# Revit family: Landscaping_Other_Axelent_Lock-Rail
name_source: partatom
category: Furniture
revit_build: Autodesk Revit 2018 (Build: 20170223_1515(x64)
units: mm (PartAtom-declared; Revit-internal decimal feet)

## family parameters
Always vertical = Yes
Cut with Voids When Loaded = No
OmniClass Number = 23.40.10.14
OmniClass Title = Exterior Specialties
Room Calculation Point = No
Shared = No
Work Plane-Based = No

## types (1)
- Bike-Up Lock rail
    AssetType = Fixed
    BIMObjectName = Landscaping_Other_Axelent_Lock-Rail
    Brand = Axelent
    Category = Cycle lockers
    Color = Galvanized
    Cost = 0 $
    CycleBollardMainMaterial = Steel, Galvanized
    Description = With this wall mounted rail a stroller can be locked and safely stored in any place. The rail is hot-dip galvanized and an appreciated detail in storage spaces.
    ExpectedLife = Years
    IfcExportAs = IfcFurnishingElementType
    IfcExportType = BOLLARD
    MainColor = Galvanized
    Manufacturer = Axelent
    ManufacturerName = Axelent
    ManufacturerURL = https://www.axelent.com
    Material = Steel
    Model = Bike-Up Lock rail
    ModelNumber = 100200
    NBSDescription = Aluminium cycle lockers
    NBSReference = 45-35-86/311
    Name = Lock-Rail
    NominalDepth = 150 mm
    NominalHeight = 204 mm
    NominalLength = 1760 mm  [stored 5.77428 ft]
    ProductDatasheet = https://www.axelent.com
    ProductInformation = With this wall mounted rail a stroller can be locked and safely stored in any place. The rail is hot-dip galvanized and an appreciated detail in storage spaces.
    Shape = Sculptured
    Size = 1760x150x204 mm
    URL = https://www.axelent.com
    Uniclass2 = Pr_40_30_20
    Uniclass2015Description = Cycle stands and lockers
    Uniclass2015Reference = Pr_40_30_21
    Version = 1
    VersionDate = 28/03/2022
    WarrantyDurationUnit = Years

note: [stored X ft] marks values corroborated as IEEE doubles in the binary element streams (Revit-internal decimal feet)

## geometry (parser evidence)
native form markers: Sweep x5
no freeform markers — native parametric forms only
